annotation { "Feature Type Name" : "Feature", "Feature Type Description" : "" }
export const myFeature = defineFeature(function(context is Context, id is Id, definition is map)
    precondition{}
    {
        {
            var Q0;
            Q0=qCreatedBy(makeId("Top.planeOp"),FACE);
            var sketch = newSketch(context, id + "F0", { "sketchPlane" : qUnion([Q0])});
            skLineSegment(sketch, "E0.top", {"start": v(-5, 600) * mm, "end": v(-808, 600) * mm});
            skLineSegment(sketch, "E0.left", {"start": v(0, 0) * mm, "end": v(0, 595) * mm});
            skLineSegment(sketch, "E0.right", {"start": v(-813, 0) * mm, "end": v(-813, 595) * mm});
            skLineSegment(sketch, "E1.0", {"start": v(-811, 2) * mm, "end": v(-811, 596) * mm});
            skLineSegment(sketch, "E1.1", {"start": v(-4, 598) * mm, "end": v(-809, 598) * mm});
            skLineSegment(sketch, "E1.2", {"start": v(-2, 2) * mm, "end": v(-2, 596) * mm});
            skPoint(sketch, "E2.visualSharp", {"position": v(-813, 600) * mm});
            skArc(sketch, "E2.filletArc", {"start": v(-808, 600) * mm, "mid": v(-811.54, 598.54) * mm, "end": v(-813, 595) * mm});
            skPoint(sketch, "E3.visualSharp", {"position": v(-811, 598) * mm});
            skArc(sketch, "E3.filletArc", {"start": v(-809, 598) * mm, "mid": v(-810.41, 597.41) * mm, "end": v(-811, 596) * mm});
            skPoint(sketch, "E4.visualSharp", {"position": v(-2, 598) * mm});
            skArc(sketch, "E4.filletArc", {"start": v(-2, 596) * mm, "mid": v(-2.59, 597.41) * mm, "end": v(-4, 598) * mm});
            skPoint(sketch, "E5.visualSharp", {"position": v(0, 600) * mm});
            skArc(sketch, "E5.filletArc", {"start": v(0, 595) * mm, "mid": v(-1.46, 598.54) * mm, "end": v(-5, 600) * mm});
            skLineSegment(sketch, "E6", {"start": v(0, 0) * mm, "end": v(-2, 0) * mm});
            skLineSegment(sketch, "E7", {"start": v(-813, 0) * mm, "end": v(-811, 0) * mm});
            skLineSegment(sketch, "E8", {"start": v(0, 0) * mm, "end": v(-811, 0) * mm});
            skLineSegment(sketch, "E9.0", {"start": v(-2, 2) * mm, "end": v(-811, 2) * mm});
            skSolve(sketch);
        }
        {
            var Q0;
            Q0 = qSketchRegion(id + "F0", true);
            extrude(context, id + "F1", {"entities" : qUnion([Q0]), "depth" : 510 * mm});
        }
        {
            var Q0;
            Q0=makeQuery(id+"F1.opExtrude","SWEPT_FACE",FACE,{"disambiguationData":[OSD([sQuery(id+"F0.wireOp",EDGE,"E0.top")])]});
            var sketch = newSketch(context, id + "F2", { "sketchPlane" : qUnion([Q0])});
            skLineSegment(sketch, "E10", {"start": v(5, 510) * mm, "end": v(5, 1210) * mm});
            skLineSegment(sketch, "E11", {"start": v(5, 1210) * mm, "end": v(585, 1210) * mm});
            skLineSegment(sketch, "E12", {"start": v(585, 1210) * mm, "end": v(808, 510) * mm});
            skPoint(sketch, "E13.orphan", {"position": v(26.17, 1210) * mm});
            skLineSegment(sketch, "E14.0", {"start": v(55, 510) * mm, "end": v(55, 1110) * mm});
            skLineSegment(sketch, "E14.2", {"start": v(559.55, 1125.18) * mm, "end": v(755.52, 510) * mm});
            skLineSegment(sketch, "E14.3", {"start": v(105, 1160) * mm, "end": v(511.9, 1160) * mm});
            skPoint(sketch, "E15.visualSharp", {"position": v(55, 1160) * mm});
            skArc(sketch, "E15.filletArc", {"start": v(105, 1160) * mm, "mid": v(69.64, 1145.36) * mm, "end": v(55, 1110) * mm});
            skPoint(sketch, "E16.visualSharp", {"position": v(548.45, 1160) * mm});
            skArc(sketch, "E16.filletArc", {"start": v(559.55, 1125.18) * mm, "mid": v(541.41, 1150.37) * mm, "end": v(511.9, 1160) * mm});
            skPoint(sketch, "E17.visualSharp", {"position": v(738.8, 562.5) * mm});
            skPoint(sketch, "E18.visualSharp", {"position": v(55, 560) * mm});
            skLineSegment(sketch, "E19", {"start": v(808, 510) * mm, "end": v(5, 510) * mm});
            skSolve(sketch);
        }
        {
            var Q0;
            Q0=makeQuery(id+"F2.imprint","IMPRINT",FACE,{"disambiguationData":[TD([[makeQuery(id+"F2.imprint","IMPRINT",EDGE,{"derivedFrom":sQuery(id+"F2.wireOp",EDGE,"E10")}),-1.0]])]});
            extrude(context, id + "F3", {"entities" : qUnion([Q0]), "oppositeDirection" : true, "depth" : 2 * mm});
        }
        {
            var Q0;
            Q0=makeQuery(id+"F3.opExtrude","SWEPT_FACE",FACE,{"disambiguationData":[OSD([sQuery(id+"F2.wireOp",EDGE,"E12")])]});
            var sketch = newSketch(context, id + "F4", { "sketchPlane" : qUnion([Q0])});
            skLineSegment(sketch, "E20.bottom", {"start": v(-598, 240.68) * mm, "end": v(0, 240.68) * mm});
            skLineSegment(sketch, "E20.left", {"start": v(-598, 240.68) * mm, "end": v(-598, 975.34) * mm});
            skPoint(sketch, "E21.visualSharp", {"position": v(-50, 375.25) * mm});
            skPoint(sketch, "E22.visualSharp", {"position": v(-515.94, 338.49) * mm});
            skPoint(sketch, "E23.orphan", {"position": v(-498, 371.42) * mm});
            skPoint(sketch, "E24.2.start.orphan", {"position": v(-299, 371.42) * mm});
            skPoint(sketch, "E21.filletArc.start.orphan", {"position": v(-100, 371.42) * mm});
            skPoint(sketch, "E25.newPointB", {"position": v(-548, 579.34) * mm});
            skLineSegment(sketch, "E26", {"start": v(-299, 240.68) * mm, "end": v(-299, 1313.82) * mm, "construction": true});
            skLineSegment(sketch, "E27.MirrorCS", {"start": v(0, 240.68) * mm, "end": v(0, 975.34) * mm});
            skLineSegment(sketch, "E28", {"start": v(-299, 829.34) * mm, "end": v(135.66, 829.34) * mm, "construction": true});
            skLineSegment(sketch, "E29.MirrorCS", {"start": v(-548, 625.51) * mm, "end": v(-548, 919.34) * mm});
            skLineSegment(sketch, "E30.MirrorCS", {"start": v(-299, 574.92) * mm, "end": v(-498, 574.92) * mm});
            skArc(sketch, "E31.MirrorCS", {"start": v(-498, 574.92) * mm, "mid": v(-533.36, 589.57) * mm, "end": v(-548, 624.92) * mm});
            skLineSegment(sketch, "E32", {"start": v(-299, 969.34) * mm, "end": v(-498, 969.34) * mm});
            skPoint(sketch, "E33.newPointA", {"position": v(-959.05, 968.75) * mm});
            skArc(sketch, "E34.filletArc", {"start": v(-498, 969.34) * mm, "mid": v(-533.36, 954.7) * mm, "end": v(-548, 919.34) * mm});
            skLineSegment(sketch, "E35", {"start": v(-299, 969.34) * mm, "end": v(-299, 1019.34) * mm});
            skLineSegment(sketch, "E36", {"start": v(-299, 1019.34) * mm, "end": v(-554, 1019.34) * mm});
            skPoint(sketch, "E37.orphan", {"position": v(-598, 975.34) * mm});
            skLineSegment(sketch, "E38", {"start": v(-598, 975.34) * mm, "end": v(-554, 1019.34) * mm});
            skLineSegment(sketch, "E39.MirrorCS", {"start": v(0, 975.34) * mm, "end": v(-44, 1019.34) * mm});
            skLineSegment(sketch, "E40.MirrorCS", {"start": v(-299, 1019.34) * mm, "end": v(-44, 1019.34) * mm});
            skLineSegment(sketch, "E41.MirrorCS", {"start": v(-299, 969.34) * mm, "end": v(-100, 969.34) * mm});
            skArc(sketch, "E42.MirrorCS", {"start": v(-100, 969.34) * mm, "mid": v(-64.64, 954.7) * mm, "end": v(-50, 919.34) * mm});
            skLineSegment(sketch, "E43.MirrorCS", {"start": v(-50, 625.51) * mm, "end": v(-50, 919.34) * mm});
            skArc(sketch, "E44.MirrorCS", {"start": v(-100, 574.92) * mm, "mid": v(-64.64, 589.57) * mm, "end": v(-50, 624.92) * mm});
            skLineSegment(sketch, "E45.MirrorCS", {"start": v(-299, 574.92) * mm, "end": v(-100, 574.92) * mm});
            skSolve(sketch);
        }
        {
            var Q0;
            Q0=makeQuery(id+"F4.imprint","IMPRINT",FACE,{"disambiguationData":[TD([[makeQuery(id+"F4.imprint","IMPRINT",EDGE,{"derivedFrom":sQuery(id+"F4.wireOp",EDGE,"E20.bottom")}),1.0]])]});
            extrude(context, id + "F5", {"entities" : qUnion([Q0]), "depth" : 2 * mm});
        }
        {
            var Q0;
            Q0=qCreatedBy(makeId("Top.planeOp"),FACE);
            var sketch = newSketch(context, id + "F6", { "sketchPlane" : qUnion([Q0])});
            skLineSegment(sketch, "E46.bottom", {"start": v(0, 0) * mm, "end": v(805, 0) * mm});
            skLineSegment(sketch, "E46.top", {"start": v(0, 600) * mm, "end": v(805, 600) * mm});
            skLineSegment(sketch, "E46.left", {"start": v(0, 0) * mm, "end": v(0, 600) * mm});
            skLineSegment(sketch, "E46.right", {"start": v(805, 0) * mm, "end": v(805, 600) * mm});
            skSolve(sketch);
        }
        {
            var Q0;
            Q0 = qSketchRegion(id + "F6", true);
            extrude(context, id + "F7", {"entities" : qUnion([Q0]), "depth" : 465 * mm, "offsetDistance" : 25 * mm});
        }
        {
            var Q0;
            Q0=makeQuery(id+"F7.opExtrude","CAP_FACE",FACE,{"disambiguationData":[OSD([sQuery(id+"F6.wireOp",EDGE,"E46.bottom"),sQuery(id+"F6.wireOp",EDGE,"E46.top"),sQuery(id+"F6.wireOp",EDGE,"E46.left"),sQuery(id+"F6.wireOp",EDGE,"E46.right")])],"isStart":true});
            var Q1;
            Q1=makeQuery(id+"F7.opExtrude","SWEPT_FACE",FACE,{"disambiguationData":[OSD([sQuery(id+"F6.wireOp",EDGE,"E46.right")])]});
            var Q2;
            Q2=makeQuery(id+"F7.opExtrude","CAP_FACE",FACE,{"disambiguationData":[OSD([sQuery(id+"F6.wireOp",EDGE,"E46.bottom"),sQuery(id+"F6.wireOp",EDGE,"E46.top"),sQuery(id+"F6.wireOp",EDGE,"E46.left"),sQuery(id+"F6.wireOp",EDGE,"E46.right")])],"isStart":false});
            var Q3;
            Q3=makeQuery(id+"F7.opExtrude","SWEPT_FACE",FACE,{"disambiguationData":[OSD([sQuery(id+"F6.wireOp",EDGE,"E46.top")])]});
            var Q4;
            Q4=makeQuery(id+"F7.opExtrude","SWEPT_FACE",FACE,{"disambiguationData":[OSD([sQuery(id+"F6.wireOp",EDGE,"E46.left")])]});
            shell(context, id + "F8", {"entities" : qUnion([Q0, Q1, Q2, Q3, Q4]), "thickness" : (2) * mm});
        }
        {
            var Q0;
            Q0=qCreatedBy(makeId("Top.planeOp"),FACE);
            var sketch = newSketch(context, id + "F9", { "sketchPlane" : qUnion([Q0])});
            skLineSegment(sketch, "E47.bottom", {"start": v(-59.87, -24.6) * mm, "end": v(-40.87, -24.6) * mm});
            skLineSegment(sketch, "E47.top", {"start": v(-59.87, -74.6) * mm, "end": v(-40.87, -74.6) * mm});
            skLineSegment(sketch, "E47.left", {"start": v(-62.87, -27.6) * mm, "end": v(-62.87, -71.6) * mm});
            skLineSegment(sketch, "E47.right", {"start": v(-37.87, -27.6) * mm, "end": v(-37.87, -71.6) * mm});
            skPoint(sketch, "E48.visualSharp", {"position": v(-62.87, -24.6) * mm});
            skArc(sketch, "E48.filletArc", {"start": v(-59.87, -24.6) * mm, "mid": v(-62, -25.49) * mm, "end": v(-62.87, -27.6) * mm});
            skPoint(sketch, "E49.visualSharp", {"position": v(-37.87, -24.6) * mm});
            skArc(sketch, "E49.filletArc", {"start": v(-37.87, -27.6) * mm, "mid": v(-38.75, -25.49) * mm, "end": v(-40.87, -24.6) * mm});
            skPoint(sketch, "E50.visualSharp", {"position": v(-37.87, -74.6) * mm});
            skArc(sketch, "E50.filletArc", {"start": v(-40.87, -74.6) * mm, "mid": v(-38.75, -73.73) * mm, "end": v(-37.87, -71.6) * mm});
            skPoint(sketch, "E51.visualSharp", {"position": v(-62.87, -74.6) * mm});
            skArc(sketch, "E51.filletArc", {"start": v(-62.87, -71.6) * mm, "mid": v(-62, -73.73) * mm, "end": v(-59.87, -74.6) * mm});
            skArc(sketch, "E52.0", {"start": v(-59.87, -26.6) * mm, "mid": v(-60.58, -26.9) * mm, "end": v(-60.87, -27.6) * mm});
            skLineSegment(sketch, "E52.1", {"start": v(-59.87, -26.6) * mm, "end": v(-40.87, -26.6) * mm});
            skLineSegment(sketch, "E52.2", {"start": v(-60.87, -27.6) * mm, "end": v(-60.87, -71.6) * mm});
            skArc(sketch, "E52.3", {"start": v(-39.87, -27.6) * mm, "mid": v(-40.17, -26.9) * mm, "end": v(-40.87, -26.6) * mm});
            skArc(sketch, "E52.4", {"start": v(-60.87, -71.6) * mm, "mid": v(-60.58, -72.31) * mm, "end": v(-59.87, -72.6) * mm});
            skLineSegment(sketch, "E52.5", {"start": v(-59.87, -72.6) * mm, "end": v(-40.87, -72.6) * mm});
            skArc(sketch, "E52.6", {"start": v(-40.87, -72.6) * mm, "mid": v(-40.17, -72.31) * mm, "end": v(-39.87, -71.6) * mm});
            skLineSegment(sketch, "E52.7", {"start": v(-39.87, -27.6) * mm, "end": v(-39.87, -71.6) * mm});
            skSolve(sketch);
        }
        {
            var Q0;
            Q0 = qSketchRegion(id + "F9", true);
            var Q1;
            Q1=makeQuery(id+"F9.imprint","IMPRINT",FACE,{"disambiguationData":[TD([[makeQuery(id+"F9.imprint","IMPRINT",EDGE,{"derivedFrom":sQuery(id+"F9.wireOp",EDGE,"E47.bottom")}),-1.0]])]});
            extrude(context, id + "F10", {"entities" : qUnion([Q0, Q1]), "depth" : 1040 * mm});
        }
        {
            var Q0;
            Q0=makeQuery(id+"F1.opExtrude","SWEPT_FACE",FACE,{"disambiguationData":[OSD([sQuery(id+"F0.wireOp",EDGE,"E7"),sQuery(id+"F0.wireOp",EDGE,"E8")])]});
            var sketch = newSketch(context, id + "F11", { "sketchPlane" : qUnion([Q0])});
            skLineSegment(sketch, "E53", {"start": v(0, 510) * mm, "end": v(-315.52, 510) * mm});
            skLineSegment(sketch, "E54", {"start": v(-538, 106.26) * mm, "end": v(-713, 106.26) * mm});
            skLineSegment(sketch, "E55", {"start": v(-763, 156.26) * mm, "end": v(-763, 510) * mm});
            skPoint(sketch, "E56.visualSharp", {"position": v(-406.5, 510) * mm});
            skPoint(sketch, "E57.visualSharp", {"position": v(-14.07, 106.26) * mm});
            skPoint(sketch, "E58.visualSharp", {"position": v(-763, 106.26) * mm});
            skArc(sketch, "E58.filletArc", {"start": v(-763, 156.26) * mm, "mid": v(-748.36, 120.9) * mm, "end": v(-713, 106.26) * mm});
            skLineSegment(sketch, "E59", {"start": v(-362.25, 477.77) * mm, "end": v(-491.26, 138.49) * mm});
            skPoint(sketch, "E60.visualSharp", {"position": v(-350, 510) * mm});
            skArc(sketch, "E60.filletArc", {"start": v(-315.52, 510) * mm, "mid": v(-343.9, 501.16) * mm, "end": v(-362.25, 477.77) * mm});
            skArc(sketch, "E61.filletArc", {"start": v(-538, 106.26) * mm, "mid": v(-509.61, 115.1) * mm, "end": v(-491.26, 138.49) * mm});
            skSolve(sketch);
        }
        {
            var Q0;
            Q0 = qSketchRegion(id + "F11", true);
            var Q1;
            Q1=makeQuery(id+"F11.imprint","IMPRINT",FACE,{"disambiguationData":[TD([[makeQuery(id+"F11.imprint","IMPRINT",EDGE,{"derivedFrom":sQuery(id+"F11.wireOp",EDGE,"Jq7AXQ9a-MJNj-Bxrc-Dwik-De4Gg8XfQ3kM")}),-1.0]])]});
            var Q2;
            Q2=makeQuery(id+"F11.imprint","IMPRINT",FACE,{"disambiguationData":[TD([[makeQuery(id+"F11.imprint","IMPRINT",EDGE,{"derivedFrom":sQuery(id+"F11.wireOp",EDGE,"E54")}),-1.0]])]});
            var Q3;
            Q3=makeQuery(id+"F1.opExtrude","SWEPT_FACE",FACE,{"disambiguationData":[OSD([sQuery(id+"F0.wireOp",EDGE,"E1.1")])]});
            extrude(context, id + "F12", {"entities" : qUnion([Q0, Q1, Q2]), "operationType" : NewBodyOperationType.REMOVE, "endBound" : BoundingType.UP_TO_SURFACE, "oppositeDirection" : true, "endBoundEntityFace" : qUnion([Q3]), "depth" : 25 * mm});
        }
        {
            var Q0;
            Q0=makeQuery(id+"F1.opExtrude","SWEPT_FACE",FACE,{"disambiguationData":[OSD([sQuery(id+"F0.wireOp",EDGE,"E0.right")])]});
            var sketch = newSketch(context, id + "F13", { "sketchPlane" : qUnion([Q0])});
            skLineSegment(sketch, "E62", {"start": v(-595, 510) * mm, "end": v(-595, 1196.55) * mm});
            skLineSegment(sketch, "E63", {"start": v(-595, 1196.55) * mm, "end": v(-595, 1203.08) * mm});
            skLineSegment(sketch, "E64", {"start": v(-595, 1203.08) * mm, "end": v(-611.4, 1194.32) * mm});
            skLineSegment(sketch, "E65", {"start": v(-611.4, 1194.32) * mm, "end": v(-537.5, 1262.48) * mm});
            skLineSegment(sketch, "E66", {"start": v(-537.5, 1262.48) * mm, "end": v(-510.53, 1287.36) * mm});
            skLineSegment(sketch, "E67", {"start": v(-297.5, 510) * mm, "end": v(-297.5, 1399.73) * mm});
            skLineSegment(sketch, "E68", {"start": v(-510.53, 1287.36) * mm, "end": v(-323.46, 1287.36) * mm});
            skLineSegment(sketch, "E69", {"start": v(-323.46, 1287.36) * mm, "end": v(-297.5, 1287.36) * mm});
            skLineSegment(sketch, "E70", {"start": v(-297.5, 1287.36) * mm, "end": v(-297.5, 1305.9) * mm});
            skLineSegment(sketch, "E71.0", {"start": v(-323.46, 1289.36) * mm, "end": v(-297.5, 1289.36) * mm});
            skLineSegment(sketch, "E71.1", {"start": v(-511.31, 1289.36) * mm, "end": v(-323.46, 1289.36) * mm});
            skLineSegment(sketch, "E71.2", {"start": v(-538.86, 1263.95) * mm, "end": v(-511.31, 1289.36) * mm});
            skLineSegment(sketch, "E72.0", {"start": v(-612.76, 1195.8) * mm, "end": v(-538.86, 1263.95) * mm});
            skLineSegment(sketch, "E73.MirrorCS", {"start": v(0, 1196.55) * mm, "end": v(0, 1203.08) * mm});
            skLineSegment(sketch, "E74.MirrorCS", {"start": v(-57.5, 1262.48) * mm, "end": v(-84.47, 1287.36) * mm});
            skLineSegment(sketch, "E75.MirrorCS", {"start": v(16.4, 1194.32) * mm, "end": v(-57.5, 1262.48) * mm});
            skLineSegment(sketch, "E76.MirrorCS", {"start": v(-56.14, 1263.95) * mm, "end": v(-83.69, 1289.36) * mm});
            skLineSegment(sketch, "E77.MirrorCS", {"start": v(17.76, 1195.8) * mm, "end": v(-56.14, 1263.95) * mm});
            skLineSegment(sketch, "E78.MirrorCS", {"start": v(-83.69, 1289.36) * mm, "end": v(-271.54, 1289.36) * mm});
            skLineSegment(sketch, "E79.MirrorCS", {"start": v(0, 1203.08) * mm, "end": v(16.4, 1194.32) * mm});
            skLineSegment(sketch, "E80.MirrorCS", {"start": v(-271.54, 1289.36) * mm, "end": v(-297.5, 1289.36) * mm});
            skLineSegment(sketch, "E81.MirrorCS", {"start": v(-84.47, 1287.36) * mm, "end": v(-271.54, 1287.36) * mm});
            skLineSegment(sketch, "E82.MirrorCS", {"start": v(-271.54, 1287.36) * mm, "end": v(-297.5, 1287.36) * mm});
            skLineSegment(sketch, "E83", {"start": v(16.4, 1194.32) * mm, "end": v(17.76, 1195.8) * mm});
            skLineSegment(sketch, "E84", {"start": v(-612.76, 1195.8) * mm, "end": v(-611.4, 1194.32) * mm});
            skSolve(sketch);
        }
        {
            var Q0;
            Q0=makeQuery(id+"F13.imprint","IMPRINT",FACE,{"disambiguationData":[TD([[makeQuery(id+"F13.imprint","IMPRINT",EDGE,{"derivedFrom":sQuery(id+"F13.wireOp",EDGE,"E74.MirrorCS")}),-1.0]])]});
            var Q1;
            Q1=makeQuery(id+"F13.imprint","IMPRINT",FACE,{"disambiguationData":[TD([[makeQuery(id+"F13.imprint","IMPRINT",EDGE,{"derivedFrom":sQuery(id+"F13.wireOp",EDGE,"E65")}),1.0]])]});
            extrude(context, id + "F14", {"entities" : qUnion([Q0, Q1]), "oppositeDirection" : true, "depth" : 600 * mm});
        }
        {
            var Q0;
            Q0=makeQuery(id+"F7.opExtrude","SWEPT_FACE",FACE,{"disambiguationData":[OSD([sQuery(id+"F6.wireOp",EDGE,"E46.bottom")])]});
            var sketch = newSketch(context, id + "F15", { "sketchPlane" : qUnion([Q0])});
            skLineSegment(sketch, "E85", {"start": v(402.5, 0) * mm, "end": v(402.5, 380) * mm, "construction": true});
            skLineSegment(sketch, "E86", {"start": v(402.5, 380) * mm, "end": v(402.5, 190) * mm, "construction": true});
            skLineSegment(sketch, "E87", {"start": v(402.5, 190) * mm, "end": v(402.5, 285) * mm});
            skLineSegment(sketch, "E88", {"start": v(402.5, 285) * mm, "end": v(102.5, 285) * mm, "construction": true});
            skLineSegment(sketch, "E89.MirrorCS", {"start": v(402.5, 285) * mm, "end": v(702.5, 285) * mm, "construction": true});
            skText(sketch, "E90", { "text": "Fixby Hall Works\nBreakdown Gang\n", "fontName": "AllertaStencil-Regular.ttf"});
            skCircle(sketch, "E91", {"center": v(402.5, 173.4) * mm, "radius": 10 * mm});
            skCircle(sketch, "E92.0.1.0", {"center": v(402.5, 53.4) * mm, "radius": 10 * mm});
            skCircle(sketch, "E92.1.0.0", {"center": v(462.5, 173.4) * mm, "radius": 10 * mm});
            skCircle(sketch, "E92.1.1.0", {"center": v(462.5, 53.4) * mm, "radius": 10 * mm});
            skCircle(sketch, "E92.2.0.0", {"center": v(522.5, 173.4) * mm, "radius": 10 * mm});
            skCircle(sketch, "E92.2.1.0", {"center": v(522.5, 53.4) * mm, "radius": 10 * mm});
            skCircle(sketch, "E92.3.0.0", {"center": v(582.5, 173.4) * mm, "radius": 10 * mm});
            skCircle(sketch, "E92.3.1.0", {"center": v(582.5, 53.4) * mm, "radius": 10 * mm});
            skCircle(sketch, "E92.4.0.0", {"center": v(642.5, 173.4) * mm, "radius": 10 * mm});
            skCircle(sketch, "E92.4.1.0", {"center": v(642.5, 53.4) * mm, "radius": 10 * mm});
            skLineSegment(sketch, "E92.direction1", {"start": v(402.5, 173.4) * mm, "end": v(462.5, 173.4) * mm, "construction": true});
            skLineSegment(sketch, "E92.direction2", {"start": v(402.5, 173.4) * mm, "end": v(402.5, 53.4) * mm, "construction": true});
            skLineSegment(sketch, "E93", {"start": v(462.5, 173.4) * mm, "end": v(402.5, 173.4) * mm});
            skLineSegment(sketch, "E94", {"start": v(432.5, 173.4) * mm, "end": v(432.5, 113.4) * mm});
            skCircle(sketch, "E95", {"center": v(432.5, 113.4) * mm, "radius": 10 * mm});
            skCircle(sketch, "E96.1.0.0", {"center": v(492.5, 113.4) * mm, "radius": 10 * mm});
            skCircle(sketch, "E96.2.0.0", {"center": v(552.5, 113.4) * mm, "radius": 10 * mm});
            skCircle(sketch, "E96.3.0.0", {"center": v(612.5, 113.4) * mm, "radius": 10 * mm});
            skCircle(sketch, "E96.4.0.0", {"center": v(672.5, 113.4) * mm, "radius": 10 * mm});
            skLineSegment(sketch, "E96.direction1", {"start": v(432.5, 113.4) * mm, "end": v(492.5, 113.4) * mm, "construction": true});
            skCircle(sketch, "E97.MirrorC", {"center": v(342.5, 173.4) * mm, "radius": 10 * mm});
            skCircle(sketch, "E98.MirrorC", {"center": v(222.5, 53.4) * mm, "radius": 10 * mm});
            skCircle(sketch, "E99.MirrorC", {"center": v(312.5, 113.4) * mm, "radius": 10 * mm});
            skCircle(sketch, "E100.MirrorC", {"center": v(252.5, 113.4) * mm, "radius": 10 * mm});
            skCircle(sketch, "E101.MirrorC", {"center": v(192.5, 113.4) * mm, "radius": 10 * mm});
            skCircle(sketch, "E102.MirrorC", {"center": v(132.5, 113.4) * mm, "radius": 10 * mm});
            skCircle(sketch, "E103.MirrorC", {"center": v(342.5, 53.4) * mm, "radius": 10 * mm});
            skCircle(sketch, "E104.MirrorC", {"center": v(282.5, 173.4) * mm, "radius": 10 * mm});
            skCircle(sketch, "E105.MirrorC", {"center": v(282.5, 53.4) * mm, "radius": 10 * mm});
            skCircle(sketch, "E106.MirrorC", {"center": v(222.5, 173.4) * mm, "radius": 10 * mm});
            skCircle(sketch, "E107.MirrorC", {"center": v(162.5, 173.4) * mm, "radius": 10 * mm});
            skCircle(sketch, "E108.MirrorC", {"center": v(162.5, 53.4) * mm, "radius": 10 * mm});
            skLineSegment(sketch, "E109.MirrorCS", {"start": v(372.5, 173.4) * mm, "end": v(372.5, 113.4) * mm});
            skLineSegment(sketch, "E110.MirrorCS", {"start": v(372.5, 113.4) * mm, "end": v(312.5, 113.4) * mm, "construction": true});
            skCircle(sketch, "E111", {"center": v(372.5, 113.4) * mm, "radius": 10 * mm});
            skLineSegment(sketch, "E112.top", {"start": v(0, 70) * mm, "end": v(35, 70) * mm});
            skLineSegment(sketch, "E112.right", {"start": v(40, 0) * mm, "end": v(40, 65) * mm});
            skPoint(sketch, "E113.visualSharp", {"position": v(40, 70) * mm});
            skArc(sketch, "E113.filletArc", {"start": v(40, 65) * mm, "mid": v(38.54, 68.54) * mm, "end": v(35, 70) * mm});
            const initialGuessF15  = {"E90": [0.1025, 0.285, 1, 0, 0.05015]};
            skSetInitialGuess(sketch, initialGuessF15);
            skSolve(sketch);
        }
        {
            var Q0;
            Q0 = qSketchRegion(id + "F15", true);
            extrude(context, id + "F16", {"entities" : qUnion([Q0]), "operationType" : NewBodyOperationType.REMOVE, "oppositeDirection" : true, "depth" : 25 * mm});
        }
        {
            var Q0;
            Q0=makeQuery(id+"F1.opExtrude","SWEPT_FACE",FACE,{"disambiguationData":[OSD([sQuery(id+"F0.wireOp",EDGE,"E0.right")])]});
            var sketch = newSketch(context, id + "F17", { "sketchPlane" : qUnion([Q0])});
            skLineSegment(sketch, "E114", {"start": v(-297.5, 500) * mm, "end": v(-297.5, 0) * mm, "construction": true});
            skLineSegment(sketch, "E115", {"start": v(-297.5, 500) * mm, "end": v(-297.5, 415) * mm, "construction": true});
            skLineSegment(sketch, "E116", {"start": v(-297.5, 415) * mm, "end": v(-595, 415) * mm, "construction": true});
            skLineSegment(sketch, "E117", {"start": v(-446.25, 415) * mm, "end": v(-595, 415) * mm});
            skLineSegment(sketch, "E118", {"start": v(-520.63, 415) * mm, "end": v(-520.63, 500) * mm, "construction": true});
            skCircle(sketch, "E119", {"center": v(-520.63, 415) * mm, "radius": 6 * mm});
            skLineSegment(sketch, "E120", {"start": v(-520.63, 415) * mm, "end": v(-595, 415) * mm});
            skCircle(sketch, "E121", {"center": v(-557.81, 415) * mm, "radius": 6 * mm});
            skLineSegment(sketch, "E122", {"start": v(-520.63, 415) * mm, "end": v(-520.63, 457.5) * mm});
            skCircle(sketch, "E123", {"center": v(-520.63, 457.5) * mm, "radius": 6 * mm});
            skSolve(sketch);
        }
        {
            var Q0;
            Q0=makeQuery(id+"F17.imprint","IMPRINT",FACE,{"disambiguationData":[TD([[makeQuery(id+"F17.imprint","IMPRINT",EDGE,{"derivedFrom":sQuery(id+"F17.wireOp",EDGE,"E123")}),-1.0]])]});
            var sketch = newSketch(context, id + "F18", { "sketchPlane" : qUnion([Q0])});
            skLineSegment(sketch, "E124.bottom", {"start": v(-742.96, 0) * mm, "end": v(-762.96, 0) * mm});
            skLineSegment(sketch, "E124.top", {"start": v(-742.96, 295) * mm, "end": v(-762.96, 295) * mm});
            skLineSegment(sketch, "E124.left", {"start": v(-742.96, 0) * mm, "end": v(-742.96, 295) * mm});
            skLineSegment(sketch, "E124.right", {"start": v(-762.96, 0) * mm, "end": v(-762.96, 295) * mm});
            skSolve(sketch);
        }
        {
            var Q0;
            Q0 = qSketchRegion(id + "F18", true);
            extrude(context, id + "F19", {"entities" : qUnion([Q0]), "depth" : 20 * mm});
        }
        {
            var Q0;
            Q0=makeQuery(id+"F19.opExtrude","SWEPT_FACE",FACE,{"disambiguationData":[OSD([sQuery(id+"F18.wireOp",EDGE,"E124.top")])]});
            var Q1;
            Q1=makeQuery(id+"F19.opExtrude","SWEPT_FACE",FACE,{"disambiguationData":[OSD([sQuery(id+"F18.wireOp",EDGE,"E124.bottom")])]});
            shell(context, id + "F20", {"entities" : qUnion([Q0, Q1]), "thickness" : 2 * mm});
        }
        {
            var Q0;
            Q0=makeQuery(id+"F19.opExtrude","CAP_FACE",FACE,{"disambiguationData":[OSD([sQuery(id+"F18.wireOp",EDGE,"E124.bottom"),sQuery(id+"F18.wireOp",EDGE,"E124.top"),sQuery(id+"F18.wireOp",EDGE,"E124.left"),sQuery(id+"F18.wireOp",EDGE,"E124.right")])],"isStart":false});
            var sketch = newSketch(context, id + "F21", { "sketchPlane" : qUnion([Q0])});
            skLineSegment(sketch, "E125.bottom", {"start": v(-828.15, 0) * mm, "end": v(-848.15, 0) * mm});
            skLineSegment(sketch, "E125.top", {"start": v(-828.15, 355) * mm, "end": v(-848.15, 355) * mm});
            skLineSegment(sketch, "E125.left", {"start": v(-828.15, 0) * mm, "end": v(-828.15, 355) * mm});
            skLineSegment(sketch, "E125.right", {"start": v(-848.15, 0) * mm, "end": v(-848.15, 355) * mm});
            skSolve(sketch);
        }
        {
            var Q0;
            Q0 = qSketchRegion(id + "F21", true);
            extrude(context, id + "F22", {"entities" : qUnion([Q0]), "depth" : 20 * mm});
        }
        {
            var Q0;
            Q0=makeQuery(id+"F22.opExtrude","SWEPT_FACE",FACE,{"disambiguationData":[OSD([sQuery(id+"F21.wireOp",EDGE,"E125.bottom")])]});
            var Q1;
            Q1=makeQuery(id+"F22.opExtrude","SWEPT_FACE",FACE,{"disambiguationData":[OSD([sQuery(id+"F21.wireOp",EDGE,"E125.top")])]});
            shell(context, id + "F23", {"entities" : qUnion([Q0, Q1]), "thickness" : 2 * mm});
        }
        {
            var Q0;
            Q0=makeQuery(id+"F17.imprint","IMPRINT",FACE,{"disambiguationData":[TD([[makeQuery(id+"F17.imprint","IMPRINT",EDGE,{"derivedFrom":sQuery(id+"F17.wireOp",EDGE,"E123")}),-1.0]])]});
            var sketch = newSketch(context, id + "F24", { "sketchPlane" : qUnion([Q0])});
            skLineSegment(sketch, "E126.bottom", {"start": v(-81.45, 523.79) * mm, "end": v(-884.45, 523.79) * mm});
            skLineSegment(sketch, "E126.top", {"start": v(-81.45, 503.79) * mm, "end": v(-884.45, 503.79) * mm});
            skLineSegment(sketch, "E126.left", {"start": v(-81.45, 523.79) * mm, "end": v(-81.45, 503.79) * mm});
            skLineSegment(sketch, "E126.right", {"start": v(-884.45, 523.79) * mm, "end": v(-884.45, 503.79) * mm});
            skSolve(sketch);
        }
        {
            var Q0;
            Q0 = qSketchRegion(id + "F24", true);
            extrude(context, id + "F25", {"entities" : qUnion([Q0]), "depth" : 20 * mm});
        }
        {
            var Q0;
            Q0=makeQuery(id+"F25.opExtrude","SWEPT_FACE",FACE,{"disambiguationData":[OSD([sQuery(id+"F24.wireOp",EDGE,"E126.left")])]});
            var Q1;
            Q1=makeQuery(id+"F25.opExtrude","SWEPT_FACE",FACE,{"disambiguationData":[OSD([sQuery(id+"F24.wireOp",EDGE,"E126.right")])]});
            shell(context, id + "F26", {"entities" : qUnion([Q0, Q1]), "thickness" : 2 * mm});
        }
        {
            var Q0;
            Q0=makeQuery(id+"F4.imprint","IMPRINT",FACE,{"disambiguationData":[TD([[makeQuery(id+"F4.imprint","IMPRINT",EDGE,{"derivedFrom":sQuery(id+"F4.wireOp",EDGE,"E20.bottom")}),1.0]])]});
            var sketch = newSketch(context, id + "F27", { "sketchPlane" : qUnion([Q0])});
            skLineSegment(sketch, "E127", {"start": v(-300.19, 969.34) * mm, "end": v(-100.35, 969.34) * mm});
            skLineSegment(sketch, "E128", {"start": v(-50.35, 919.34) * mm, "end": v(-50.35, 569.34) * mm});
            skLineSegment(sketch, "E129", {"start": v(-100.35, 519.34) * mm, "end": v(-300.19, 519.34) * mm});
            skPoint(sketch, "E130.visualSharp", {"position": v(-50.35, 969.34) * mm});
            skArc(sketch, "E130.filletArc", {"start": v(-50.35, 919.34) * mm, "mid": v(-65, 954.7) * mm, "end": v(-100.35, 969.34) * mm});
            skPoint(sketch, "E131.visualSharp", {"position": v(-50.35, 519.34) * mm});
            skArc(sketch, "E131.filletArc", {"start": v(-100.35, 519.34) * mm, "mid": v(-65, 533.98) * mm, "end": v(-50.35, 569.34) * mm});
            skLineSegment(sketch, "E132", {"start": v(-300.19, 969.34) * mm, "end": v(-300.19, 519.34) * mm, "construction": true});
            skLineSegment(sketch, "E133.MirrorCS", {"start": v(-297.81, 969.34) * mm, "end": v(-497.65, 969.34) * mm});
            skArc(sketch, "E134.MirrorCS", {"start": v(-547.65, 919.34) * mm, "mid": v(-533, 954.7) * mm, "end": v(-497.65, 969.34) * mm});
            skLineSegment(sketch, "E135.MirrorCS", {"start": v(-547.65, 919.34) * mm, "end": v(-547.65, 569.34) * mm});
            skArc(sketch, "E136.MirrorCS", {"start": v(-497.65, 519.34) * mm, "mid": v(-533, 533.98) * mm, "end": v(-547.65, 569.34) * mm});
            skLineSegment(sketch, "E137.MirrorCS", {"start": v(-497.65, 519.34) * mm, "end": v(-297.81, 519.34) * mm});
            skSolve(sketch);
        }
        {
            var Q0;
            Q0 = qSketchRegion(id + "F27", true);
            extrude(context, id + "F28", {"entities" : qUnion([Q0]), "operationType" : NewBodyOperationType.ADD, "depth" : 25 * mm});
        }
        {
            var Q0;
            {var subQ2=sQuery(id+"F27.wireOp",EDGE,"E127");Q0=makeQuery(id+"F27.imprint","IMPRINT",FACE,{"disambiguationData":[TD([[makeQuery(id+"F27.imprint","IMPRINT",EDGE,{"derivedFrom":subQ2}),-1.0]])]});}
            extrude(context, id + "F29", {"entities" : qUnion([Q0]), "operationType" : NewBodyOperationType.REMOVE, "endBound" : BoundingType.THROUGH_ALL, "depth" : 25 * mm});
        }
        {
            var Q0;
            Q0=makeQuery(id+"F5.opExtrude","SWEPT_BODY",BODY,{"disambiguationData":[OSD([sQuery(id+"F4.wireOp",EDGE,"E20.bottom"),sQuery(id+"F4.wireOp",EDGE,"E20.left"),sQuery(id+"F4.wireOp",EDGE,"E27.MirrorCS"),sQuery(id+"F4.wireOp",EDGE,"E36"),sQuery(id+"F4.wireOp",EDGE,"E38"),sQuery(id+"F4.wireOp",EDGE,"E39.MirrorCS"),sQuery(id+"F4.wireOp",EDGE,"E40.MirrorCS")])]});
            transform(context, id + "F30", {"entities" : qUnion([Q0]), "transformType" : TransformType.TRANSLATION_3D, "dx" : 150 * mm, "dy" : 0 * mm, "dz" : 0 * mm, "makeCopy" : true});
        }
        {
            var Q0;
            Q0=makeQuery(id+"F30.opPattern","COPY",FACE,{"derivedFrom":makeQuery(id+"F5.opExtrude","CAP_FACE",FACE,{"disambiguationData":[OSD([sQuery(id+"F4.wireOp",EDGE,"E20.bottom"),sQuery(id+"F4.wireOp",EDGE,"E20.left"),sQuery(id+"F4.wireOp",EDGE,"E27.MirrorCS"),sQuery(id+"F4.wireOp",EDGE,"E36"),sQuery(id+"F4.wireOp",EDGE,"E38"),sQuery(id+"F4.wireOp",EDGE,"E39.MirrorCS"),sQuery(id+"F4.wireOp",EDGE,"E40.MirrorCS")])],"isStart":true}),"instanceName":"1"});
            var sketch = newSketch(context, id + "F31", { "sketchPlane" : qUnion([Q0])});
            skLineSegment(sketch, "E138", {"start": v(50.35, 614.87) * mm, "end": v(50.35, 702.03) * mm});
            skLineSegment(sketch, "E139", {"start": v(100.35, 702.03) * mm, "end": v(497.65, 702.03) * mm});
            skLineSegment(sketch, "E140", {"start": v(547.65, 702.03) * mm, "end": v(547.65, 614.87) * mm});
            skLineSegment(sketch, "E141", {"start": v(100.35, 564.87) * mm, "end": v(497.65, 564.87) * mm});
            skArc(sketch, "E142.filletArc", {"start": v(497.65, 564.87) * mm, "mid": v(533, 579.51) * mm, "end": v(547.65, 614.87) * mm});
            skPoint(sketch, "E143.visualSharp", {"position": v(50.35, 564.87) * mm});
            skArc(sketch, "E143.filletArc", {"start": v(50.35, 614.87) * mm, "mid": v(65, 579.51) * mm, "end": v(100.35, 564.87) * mm});
            skPoint(sketch, "E144.visualSharp", {"position": v(50.35, 702.03) * mm});
            skArc(sketch, "E144.filletArc", {"start": v(50.35, 752.03) * mm, "mid": v(65, 716.67) * mm, "end": v(100.35, 702.03) * mm});
            skPoint(sketch, "E145.visualSharp", {"position": v(547.65, 702.03) * mm});
            skArc(sketch, "E145.filletArc", {"start": v(497.65, 702.03) * mm, "mid": v(533, 716.67) * mm, "end": v(547.65, 752.03) * mm});
            skSolve(sketch);
        }
        {
            var Q0;
            Q0=makeQuery(id+"F31.imprint","IMPRINT",FACE,{"disambiguationData":[TD([[makeQuery(id+"F31.imprint","IMPRINT",EDGE,{"derivedFrom":sQuery(id+"F31.wireOp",EDGE,"E138")}),1.0]])]});
            extrude(context, id + "F32", {"entities" : qUnion([Q0]), "operationType" : NewBodyOperationType.ADD, "oppositeDirection" : true, "depth" : 2 * mm});
        }
        {
            var Q0;
            Q0=makeQuery(id+"F32.boolean.opBoolean","MERGE",FACE,{"derivedFrom":[makeQuery(id+"F30.opPattern","COPY",FACE,{"derivedFrom":makeQuery(id+"F5.opExtrude","CAP_FACE",FACE,{"disambiguationData":[OSD([sQuery(id+"F4.wireOp",EDGE,"E20.bottom"),sQuery(id+"F4.wireOp",EDGE,"E20.left"),sQuery(id+"F4.wireOp",EDGE,"E27.MirrorCS"),sQuery(id+"F4.wireOp",EDGE,"E36"),sQuery(id+"F4.wireOp",EDGE,"E38"),sQuery(id+"F4.wireOp",EDGE,"E39.MirrorCS"),sQuery(id+"F4.wireOp",EDGE,"E40.MirrorCS")])],"isStart":true}),"instanceName":"1"}),makeQuery(id+"F32.opExtrude","CAP_FACE",FACE,{"disambiguationData":[OSD([sQuery(id+"F27.wireOp",EDGE,"E128"),sQuery(id+"F27.wireOp",EDGE,"E135.MirrorCS"),sQuery(id+"F31.wireOp",EDGE,"E138"),sQuery(id+"F31.wireOp",EDGE,"E139"),sQuery(id+"F31.wireOp",EDGE,"E140"),sQuery(id+"F31.wireOp",EDGE,"E141"),sQuery(id+"F31.wireOp",EDGE,"E142.filletArc"),sQuery(id+"F31.wireOp",EDGE,"E143.filletArc"),sQuery(id+"F31.wireOp",EDGE,"E144.filletArc"),sQuery(id+"F31.wireOp",EDGE,"E145.filletArc")])],"isStart":true})]});
            var sketch = newSketch(context, id + "F33", { "sketchPlane" : qUnion([Q0])});
            skLineSegment(sketch, "E146.bottom", {"start": v(0, 286.2) * mm, "end": v(598, 286.2) * mm});
            skLineSegment(sketch, "E146.top", {"start": v(0, 321.2) * mm, "end": v(598, 321.2) * mm});
            skLineSegment(sketch, "E146.left", {"start": v(0, 286.2) * mm, "end": v(0, 321.2) * mm});
            skLineSegment(sketch, "E146.right", {"start": v(598, 286.2) * mm, "end": v(598, 321.2) * mm});
            skSolve(sketch);
        }
        {
            var Q0;
            Q0 = qSketchRegion(id + "F33", true);
            extrude(context, id + "F34", {"entities" : qUnion([Q0]), "operationType" : NewBodyOperationType.REMOVE, "oppositeDirection" : true, "depth" : 25 * mm});
        }
        {
            var Q0;
            Q0=qCreatedBy(makeId("Right.planeOp"),FACE);
            var sketch = newSketch(context, id + "F35", { "sketchPlane" : qUnion([Q0])});
            skLineSegment(sketch, "E147.top", {"start": v(-624.5, 48.19) * mm, "end": v(-574.5, 48.19) * mm});
            skLineSegment(sketch, "E148", {"start": v(-624.5, 795.18) * mm, "end": v(-574.5, 795.18) * mm, "construction": true});
            skLineSegment(sketch, "E149", {"start": v(-624.5, 795.18) * mm, "end": v(-624.5, 785.18) * mm, "construction": true});
            skLineSegment(sketch, "E150", {"start": v(-599.5, 898.19) * mm, "end": v(-599.5, 848.19) * mm, "construction": true});
            skLineSegment(sketch, "E151", {"start": v(-599.5, 848.19) * mm, "end": v(-599.5, 795.18) * mm, "construction": true});
            skLineSegment(sketch, "E152", {"start": v(-599.5, 795.18) * mm, "end": v(-599.5, 785.18) * mm, "construction": true});
            skLineSegment(sketch, "E153", {"start": v(-599.5, 785.18) * mm, "end": v(-599.5, 735.18) * mm, "construction": true});
            skLineSegment(sketch, "E154", {"start": v(-599.5, 735.18) * mm, "end": v(-599.5, 725.18) * mm, "construction": true});
            skLineSegment(sketch, "E155", {"start": v(-599.5, 725.18) * mm, "end": v(-599.5, 675.18) * mm, "construction": true});
            skLineSegment(sketch, "E156", {"start": v(-599.5, 675.18) * mm, "end": v(-599.5, 665.18) * mm, "construction": true});
            skLineSegment(sketch, "E157", {"start": v(-599.5, 665.18) * mm, "end": v(-599.5, 615.18) * mm, "construction": true});
            skLineSegment(sketch, "E158", {"start": v(-599.5, 615.18) * mm, "end": v(-599.5, 565.18) * mm, "construction": true});
            skLineSegment(sketch, "E159", {"start": v(-599.5, 565.18) * mm, "end": v(-599.5, 515.18) * mm, "construction": true});
            skPoint(sketch, "E159.endSnap0", {"position": v(-599.5, 640.18) * mm});
            skLineSegment(sketch, "E160", {"start": v(-599.5, 515.18) * mm, "end": v(-599.5, 505.18) * mm, "construction": true});
            skLineSegment(sketch, "E161", {"start": v(-599.5, 505.18) * mm, "end": v(-599.5, 455.18) * mm, "construction": true});
            skLineSegment(sketch, "E162", {"start": v(-599.5, 455.18) * mm, "end": v(-599.5, 445.18) * mm, "construction": true});
            skLineSegment(sketch, "E163", {"start": v(-599.5, 445.18) * mm, "end": v(-599.5, 395.18) * mm, "construction": true});
            skLineSegment(sketch, "E164", {"start": v(-599.5, 395.18) * mm, "end": v(-599.5, 385.18) * mm, "construction": true});
            skLineSegment(sketch, "E165", {"start": v(-599.5, 385.18) * mm, "end": v(-599.5, 335.18) * mm, "construction": true});
            skLineSegment(sketch, "E166", {"start": v(-599.5, 335.18) * mm, "end": v(-599.5, 325.18) * mm, "construction": true});
            skLineSegment(sketch, "E167", {"start": v(-599.5, 325.18) * mm, "end": v(-599.5, 275.18) * mm, "construction": true});
            skLineSegment(sketch, "E168", {"start": v(-599.5, 275.18) * mm, "end": v(-599.5, 265.18) * mm, "construction": true});
            skLineSegment(sketch, "E169", {"start": v(-599.5, 265.18) * mm, "end": v(-599.5, 215.18) * mm, "construction": true});
            skLineSegment(sketch, "E170", {"start": v(-599.5, 215.18) * mm, "end": v(-599.5, 205.18) * mm, "construction": true});
            skLineSegment(sketch, "E171", {"start": v(-599.5, 205.18) * mm, "end": v(-599.5, 155.18) * mm, "construction": true});
            skLineSegment(sketch, "E172", {"start": v(-599.5, 155.18) * mm, "end": v(-599.5, 145.18) * mm, "construction": true});
            skText(sketch, "E173", { "text": "K", "fontName": "AllertaStencil-Regular.ttf"});
            skText(sketch, "E174", { "text": "i", "fontName": "OpenSans-Regular.ttf"});
            skText(sketch, "E175", { "text": "n", "fontName": "AllertaStencil-Regular.ttf"});
            skText(sketch, "E176", { "text": "g", "fontName": "AllertaStencil-Regular.ttf"});
            skText(sketch, "E177", { "text": "R", "fontName": "AllertaStencil-Regular.ttf"});
            skText(sketch, "E178", { "text": "i", "fontName": "AllertaStencil-Regular.ttf"});
            skText(sketch, "E179", { "text": "c", "fontName": "AllertaStencil-Regular.ttf"});
            skText(sketch, "E180", { "text": "h", "fontName": "AllertaStencil-Regular.ttf"});
            skText(sketch, "E181", { "text": "a", "fontName": "AllertaStencil-Regular.ttf"});
            skText(sketch, "E182", { "text": "r", "fontName": "AllertaStencil-Regular.ttf"});
            skText(sketch, "E183", { "text": "d", "fontName": "AllertaStencil-Regular.ttf"});
            skPoint(sketch, "E184.orphan", {"position": v(-699.5, 898.19) * mm});
            skPoint(sketch, "E185.orphan", {"position": v(-499.5, 898.19) * mm});
            skLineSegment(sketch, "E186", {"start": v(-624.5, 873.19) * mm, "end": v(-624.5, 48.19) * mm});
            skLineSegment(sketch, "E187.MirrorCS", {"start": v(-574.5, 898.19) * mm, "end": v(-574.5, 48.19) * mm});
            skPoint(sketch, "E188.orphan", {"position": v(-649.5, 48.19) * mm});
            skPoint(sketch, "E189.MirrorCS.end.orphan", {"position": v(-549.5, 48.19) * mm});
            skPoint(sketch, "E190.trimOffspring.end.orphan", {"position": v(-549.5, 898.19) * mm});
            skLineSegment(sketch, "E191", {"start": v(-624.5, 873.19) * mm, "end": v(-574.5, 873.19) * mm});
            skPoint(sketch, "E191.startSnap0", {"position": v(-599.5, 873.19) * mm});
            skPoint(sketch, "E147.bottom.end.orphan", {"position": v(-624.5, 898.19) * mm});
            skPoint(sketch, "E147.bottom.start.orphan", {"position": v(-649.5, 898.19) * mm});
            const initialGuessF35  = {"E173": [-0.62272, 0.79518, 1, 0, 0.05078], "E174": [-0.609, 0.73518, 1, 0, 0.05], "E175": [-0.62047, 0.67518, 1, 0, 0.05], "E176": [-0.6209, 0.61518, 1, 0, 0.05], "E177": [-0.6217, 0.51518, 1, 0, 0.05], "E178": [-0.60934, 0.45518, 1, 0, 0.05], "E179": [-0.6195, 0.39518, 1, 0, 0.05], "E180": [-0.62082, 0.33518, 1, 0, 0.05], "E181": [-0.62, 0.27518, 1, 0, 0.05], "E182": [-0.61566, 0.21518, 1, 0, 0.05], "E183": [-0.6204, 0.15518, 1, 0, 0.05]};
            skSetInitialGuess(sketch, initialGuessF35);
            skSolve(sketch);
        }
        {
            var Q0;
            Q0 = qSketchRegion(id + "F35", true);
            extrude(context, id + "F36", {"entities" : qUnion([Q0]), "oppositeDirection" : true, "depth" : 50 * mm});
        }
        {
            var Q0;
            Q0=makeQuery(id+"F36.opExtrude","SWEPT_FACE",FACE,{"disambiguationData":[OSD([sQuery(id+"F35.wireOp",EDGE,"E191")])]});
            var sketch = newSketch(context, id + "F37", { "sketchPlane" : qUnion([Q0])});
            skLineSegment(sketch, "E192.0", {"start": v(-50, -622.5) * mm, "end": v(-2, -622.5) * mm});
            skLineSegment(sketch, "E192.1", {"start": v(-2, -622.5) * mm, "end": v(-2, -576.5) * mm});
            skLineSegment(sketch, "E192.2", {"start": v(-50, -576.5) * mm, "end": v(-2, -576.5) * mm});
            skLineSegment(sketch, "E193", {"start": v(-50, -576.5) * mm, "end": v(-50, -622.5) * mm});
            skSolve(sketch);
        }
        {
            var Q0;
            Q0 = qSketchRegion(id + "F37", true);
            extrude(context, id + "F38", {"entities" : qUnion([Q0]), "operationType" : NewBodyOperationType.REMOVE, "endBound" : BoundingType.THROUGH_ALL, "oppositeDirection" : true, "depth" : 25 * mm});
        }
        {
            var Q0;
            Q0=makeQuery(id+"F7.opExtrude","SWEPT_FACE",FACE,{"disambiguationData":[OSD([sQuery(id+"F6.wireOp",EDGE,"E46.bottom")])]});
            var sketch = newSketch(context, id + "F39", { "sketchPlane" : qUnion([Q0])});
            skLineSegment(sketch, "E194.bottom", {"start": v(-1, 0) * mm, "end": v(760, 0) * mm});
            skLineSegment(sketch, "E194.top", {"start": v(-1, 465) * mm, "end": v(800, 465) * mm});
            skLineSegment(sketch, "E194.left", {"start": v(-3, 2) * mm, "end": v(-3, 463) * mm});
            skLineSegment(sketch, "E194.right", {"start": v(802, 75) * mm, "end": v(802, 463) * mm});
            skText(sketch, "E195", { "text": "Fixby Park Works", "fontName": "AllertaStencil-Regular.ttf"});
            skLineSegment(sketch, "E196", {"start": v(402.5, 465) * mm, "end": v(401.32, 0) * mm, "construction": true});
            skText(sketch, "E197", { "text": "Breakdown Gang", "fontName": "AllertaStencil-Regular.ttf"});
            skText(sketch, "E198", { "text": "Crane No1", "fontName": "AllertaStencil-Regular.ttf"});
            skPoint(sketch, "E199.visualSharp", {"position": v(802, 465) * mm});
            skArc(sketch, "E199.filletArc", {"start": v(802, 463) * mm, "mid": v(801.41, 464.41) * mm, "end": v(800, 465) * mm});
            skPoint(sketch, "E200.visualSharp", {"position": v(802, 0) * mm});
            skPoint(sketch, "E201.visualSharp", {"position": v(-3, 465) * mm});
            skArc(sketch, "E201.filletArc", {"start": v(-1, 465) * mm, "mid": v(-2.41, 464.41) * mm, "end": v(-3, 463) * mm});
            skPoint(sketch, "E202.MirrorP", {"position": v(763, 68.17) * mm});
            skPoint(sketch, "E203.MirrorP", {"position": v(806, 67.96) * mm});
            skPoint(sketch, "E204.MirrorP", {"position": v(762.64, -1.83) * mm});
            skPoint(sketch, "E205.orphan", {"position": v(-3, 70) * mm});
            skPoint(sketch, "E206.orphan", {"position": v(40, 0) * mm});
            skPoint(sketch, "E207.visualSharp", {"position": v(-3, 0) * mm});
            skArc(sketch, "E207.filletArc", {"start": v(-3, 2) * mm, "mid": v(-2.41, 0.59) * mm, "end": v(-1, 0) * mm});
            skLineSegment(sketch, "E208", {"start": v(800, 73) * mm, "end": v(767, 73) * mm});
            skLineSegment(sketch, "E209", {"start": v(762, 68) * mm, "end": v(762, 2) * mm});
            skPoint(sketch, "E210.newPointA", {"position": v(762, 3) * mm});
            skArc(sketch, "E210.filletArc", {"start": v(760, 0) * mm, "mid": v(761.41, 0.59) * mm, "end": v(762, 2) * mm});
            skPoint(sketch, "E211.newPointB", {"position": v(802, 73) * mm});
            skArc(sketch, "E211.filletArc", {"start": v(800, 73) * mm, "mid": v(801.41, 73.59) * mm, "end": v(802, 75) * mm});
            skPoint(sketch, "E212.visualSharp", {"position": v(762, 73) * mm});
            skArc(sketch, "E212.filletArc", {"start": v(767, 73) * mm, "mid": v(763.46, 71.54) * mm, "end": v(762, 68) * mm});
            const initialGuessF39  = {"E195": [0.03673, 0.33513, 1, 0, 0.06], "E197": [0.04793, 0.22513, 1, 0, 0.06], "E198": [0.19516, 0.11513, 1, 0, 0.06]};
            skSetInitialGuess(sketch, initialGuessF39);
            skSolve(sketch);
        }
        {
            var Q0;
            Q0 = qSketchRegion(id + "F39", true);
            extrude(context, id + "F40", {"entities" : qUnion([Q0]), "depth" : 2 * mm, "offsetDistance" : 25 * mm});
        }
        {
            var Q0;
            Q0=qCreatedBy(makeId("Front.planeOp"),FACE);
            var sketch = newSketch(context, id + "F41", { "sketchPlane" : qUnion([Q0])});
            skLineSegment(sketch, "E213.bottom", {"start": v(1208.11, 15.86) * mm, "end": v(1794.11, 15.86) * mm});
            skLineSegment(sketch, "E213.top", {"start": v(1208.11, -389.14) * mm, "end": v(1794.11, -389.14) * mm});
            skLineSegment(sketch, "E213.left", {"start": v(1206.11, 13.86) * mm, "end": v(1206.11, -387.14) * mm});
            skLineSegment(sketch, "E213.right", {"start": v(1796.11, 13.86) * mm, "end": v(1796.11, -387.14) * mm});
            skPoint(sketch, "E214.visualSharp", {"position": v(1206.11, 15.86) * mm});
            skArc(sketch, "E214.filletArc", {"start": v(1208.11, 15.86) * mm, "mid": v(1206.7, 15.27) * mm, "end": v(1206.11, 13.86) * mm});
            skPoint(sketch, "E215.visualSharp", {"position": v(1796.11, 15.86) * mm});
            skArc(sketch, "E215.filletArc", {"start": v(1796.11, 13.86) * mm, "mid": v(1795.53, 15.27) * mm, "end": v(1794.11, 15.86) * mm});
            skPoint(sketch, "E216.visualSharp", {"position": v(1796.11, -389.14) * mm});
            skArc(sketch, "E216.filletArc", {"start": v(1794.11, -389.14) * mm, "mid": v(1795.53, -388.56) * mm, "end": v(1796.11, -387.14) * mm});
            skPoint(sketch, "E217.visualSharp", {"position": v(1206.11, -389.14) * mm});
            skArc(sketch, "E217.filletArc", {"start": v(1206.11, -387.14) * mm, "mid": v(1206.7, -388.56) * mm, "end": v(1208.11, -389.14) * mm});
            skLineSegment(sketch, "E218", {"start": v(1206.11, -139.14) * mm, "end": v(1276.11, -139.14) * mm, "construction": true});
            skLineSegment(sketch, "E219", {"start": v(1276.11, -139.14) * mm, "end": v(1276.11, -389.14) * mm, "construction": true});
            skLineSegment(sketch, "E220.bottom", {"start": v(1281.11, -139.14) * mm, "end": v(1301.11, -139.14) * mm});
            skLineSegment(sketch, "E220.top", {"start": v(1281.11, -49.14) * mm, "end": v(1301.11, -49.14) * mm});
            skLineSegment(sketch, "E220.left", {"start": v(1276.11, -134.14) * mm, "end": v(1276.11, -54.14) * mm});
            skLineSegment(sketch, "E220.right", {"start": v(1306.11, -134.14) * mm, "end": v(1306.11, -54.14) * mm});
            skPoint(sketch, "E221.visualSharp", {"position": v(1276.11, -49.14) * mm});
            skArc(sketch, "E221.filletArc", {"start": v(1281.11, -49.14) * mm, "mid": v(1277.58, -50.6) * mm, "end": v(1276.11, -54.14) * mm});
            skPoint(sketch, "E222.visualSharp", {"position": v(1276.11, -139.14) * mm});
            skArc(sketch, "E222.filletArc", {"start": v(1276.11, -134.14) * mm, "mid": v(1277.58, -137.68) * mm, "end": v(1281.11, -139.14) * mm});
            skPoint(sketch, "E223.visualSharp", {"position": v(1306.11, -139.14) * mm});
            skArc(sketch, "E223.filletArc", {"start": v(1301.11, -139.14) * mm, "mid": v(1304.65, -137.68) * mm, "end": v(1306.11, -134.14) * mm});
            skPoint(sketch, "E224.visualSharp", {"position": v(1306.11, -49.14) * mm});
            skArc(sketch, "E224.filletArc", {"start": v(1306.11, -54.14) * mm, "mid": v(1304.65, -50.6) * mm, "end": v(1301.11, -49.14) * mm});
            skSolve(sketch);
        }
        {
            var Q0;
            Q0 = qSketchRegion(id + "F41", true);
            extrude(context, id + "F42", {"entities" : qUnion([Q0]), "depth" : 2 * mm, "offsetDistance" : 25 * mm});
        }
        {
            var Q0;
            Q0=qCreatedBy(makeId("Front.planeOp"),FACE);
            var sketch = newSketch(context, id + "F43", { "sketchPlane" : qUnion([Q0])});
            skLineSegment(sketch, "E225.bottom", {"start": v(250.22, 108.67) * mm, "end": v(788.15, 108.67) * mm});
            skLineSegment(sketch, "E225.top", {"start": v(208.15, -353.33) * mm, "end": v(788.15, -353.33) * mm});
            skLineSegment(sketch, "E225.left", {"start": v(203.15, 61.6) * mm, "end": v(203.15, -348.33) * mm});
            skLineSegment(sketch, "E225.right", {"start": v(793.15, 103.67) * mm, "end": v(793.15, -348.33) * mm});
            skPoint(sketch, "E226.visualSharp", {"position": v(203.15, -353.33) * mm});
            skArc(sketch, "E226.filletArc", {"start": v(203.15, -348.33) * mm, "mid": v(204.61, -351.87) * mm, "end": v(208.15, -353.33) * mm});
            skPoint(sketch, "E227.visualSharp", {"position": v(793.15, -353.33) * mm});
            skArc(sketch, "E227.filletArc", {"start": v(788.15, -353.33) * mm, "mid": v(791.68, -351.87) * mm, "end": v(793.15, -348.33) * mm});
            skPoint(sketch, "E228.visualSharp", {"position": v(793.15, 108.67) * mm});
            skArc(sketch, "E228.filletArc", {"start": v(793.15, 103.67) * mm, "mid": v(791.68, 107.2) * mm, "end": v(788.15, 108.67) * mm});
            skLineSegment(sketch, "E229", {"start": v(204.61, 65.13) * mm, "end": v(246.68, 107.2) * mm});
            skArc(sketch, "E230.filletArc", {"start": v(250.22, 108.67) * mm, "mid": v(248.3, 108.29) * mm, "end": v(246.68, 107.2) * mm});
            skPoint(sketch, "E231.visualSharp", {"position": v(203.15, 63.67) * mm});
            skArc(sketch, "E231.filletArc", {"start": v(204.61, 65.13) * mm, "mid": v(203.53, 63.51) * mm, "end": v(203.15, 61.6) * mm});
            skSolve(sketch);
        }
        {
            var Q0;
            Q0 = qSketchRegion(id + "F43", true);
            extrude(context, id + "F44", {"entities" : qUnion([Q0]), "depth" : 2 * mm, "offsetDistance" : 25 * mm});
        }
        {
            var Q0;
            Q0=qCreatedBy(makeId("Front.planeOp"),FACE);
            var sketch = newSketch(context, id + "F45", { "sketchPlane" : qUnion([Q0])});
            skLineSegment(sketch, "E232.bottom", {"start": v(-1223.5, 239.15) * mm, "end": v(-508.5, 239.15) * mm});
            skLineSegment(sketch, "E232.top", {"start": v(-1223.5, -190.85) * mm, "end": v(-508.5, -190.85) * mm});
            skLineSegment(sketch, "E232.left", {"start": v(-1228.5, 234.15) * mm, "end": v(-1228.5, -185.85) * mm});
            skLineSegment(sketch, "E232.right", {"start": v(-488.5, 219.15) * mm, "end": v(-488.5, -170.85) * mm});
            skPoint(sketch, "E233.visualSharp", {"position": v(-1228.5, 239.15) * mm});
            skArc(sketch, "E233.filletArc", {"start": v(-1223.5, 239.15) * mm, "mid": v(-1227.04, 237.69) * mm, "end": v(-1228.5, 234.15) * mm});
            skPoint(sketch, "E234.visualSharp", {"position": v(-1228.5, -190.85) * mm});
            skArc(sketch, "E234.filletArc", {"start": v(-1228.5, -185.85) * mm, "mid": v(-1227.04, -189.38) * mm, "end": v(-1223.5, -190.85) * mm});
            skPoint(sketch, "E235.visualSharp", {"position": v(-488.5, -190.85) * mm});
            skArc(sketch, "E235.filletArc", {"start": v(-508.5, -190.85) * mm, "mid": v(-494.36, -184.99) * mm, "end": v(-488.5, -170.85) * mm});
            skPoint(sketch, "E236.visualSharp", {"position": v(-488.5, 239.15) * mm});
            skArc(sketch, "E236.filletArc", {"start": v(-488.5, 219.15) * mm, "mid": v(-494.36, 233.3) * mm, "end": v(-508.5, 239.15) * mm});
            skText(sketch, "E237", { "text": "Richard\nOastler", "fontName": "AllertaStencil-Regular.ttf"});
            const initialGuessF45  = {"E237": [-0.85591, 0.1096, 1, 0, 0.05]};
            skSetInitialGuess(sketch, initialGuessF45);
            skSolve(sketch);
        }
        {
            var Q0;
            Q0 = qSketchRegion(id + "F45", true);
            extrude(context, id + "F46", {"entities" : qUnion([Q0]), "depth" : 2 * mm, "offsetDistance" : 25 * mm});
        }
        {
            var Q0;
            Q0=qCreatedBy(makeId("Front.planeOp"),FACE);
            var sketch = newSketch(context, id + "F47", { "sketchPlane" : qUnion([Q0])});
            skLineSegment(sketch, "E238.bottom", {"start": v(-2122.51, 103.14) * mm, "end": v(-1622.51, 103.14) * mm});
            skLineSegment(sketch, "E238.top", {"start": v(-2122.51, -466.86) * mm, "end": v(-1622.51, -466.86) * mm});
            skLineSegment(sketch, "E238.left", {"start": v(-2142.51, 83.14) * mm, "end": v(-2142.51, -446.86) * mm});
            skLineSegment(sketch, "E238.right", {"start": v(-1602.51, 83.14) * mm, "end": v(-1602.51, -446.86) * mm});
            skPoint(sketch, "E239.visualSharp", {"position": v(-2142.51, 103.14) * mm});
            skArc(sketch, "E239.filletArc", {"start": v(-2122.51, 103.14) * mm, "mid": v(-2136.65, 97.28) * mm, "end": v(-2142.51, 83.14) * mm});
            skPoint(sketch, "E240.visualSharp", {"position": v(-2142.51, -466.86) * mm});
            skArc(sketch, "E240.filletArc", {"start": v(-2142.51, -446.86) * mm, "mid": v(-2136.65, -461) * mm, "end": v(-2122.51, -466.86) * mm});
            skPoint(sketch, "E241.visualSharp", {"position": v(-1602.51, -466.86) * mm});
            skArc(sketch, "E241.filletArc", {"start": v(-1622.51, -466.86) * mm, "mid": v(-1608.37, -461) * mm, "end": v(-1602.51, -446.86) * mm});
            skPoint(sketch, "E242.visualSharp", {"position": v(-1602.51, 103.14) * mm});
            skArc(sketch, "E242.filletArc", {"start": v(-1602.51, 83.14) * mm, "mid": v(-1608.37, 97.28) * mm, "end": v(-1622.51, 103.14) * mm});
            skLineSegment(sketch, "E243", {"start": v(-1872.51, 103.14) * mm, "end": v(-1872.51, -466.86) * mm, "construction": true});
            skText(sketch, "E244", { "text": "No1", "fontName": "AllertaStencil-Regular.ttf"});
            const initialGuessF47  = {"E244": [-1.99354, -0.18186, 1, 0, 0.1]};
            skSetInitialGuess(sketch, initialGuessF47);
            skSolve(sketch);
        }
        {
            var Q0;
            Q0 = qSketchRegion(id + "F47", true);
            extrude(context, id + "F48", {"entities" : qUnion([Q0]), "depth" : 2 * mm, "offsetDistance" : 25 * mm});
        }
        {
            var Q0;
            Q0=makeQuery(id+"F48.opExtrude","CAP_FACE",FACE,{"disambiguationData":[OSD([sQuery(id+"F47.wireOp",EDGE,"E238.bottom"),sQuery(id+"F47.wireOp",EDGE,"E238.top"),sQuery(id+"F47.wireOp",EDGE,"E238.left"),sQuery(id+"F47.wireOp",EDGE,"E238.right"),sQuery(id+"F47.wireOp",EDGE,"E239.filletArc"),sQuery(id+"F47.wireOp",EDGE,"E240.filletArc"),sQuery(id+"F47.wireOp",EDGE,"E241.filletArc"),sQuery(id+"F47.wireOp",EDGE,"E242.filletArc"),sQuery(id+"F47.wireOp",EDGE,"E244.sketch_text.stroke-0"),sQuery(id+"F47.wireOp",EDGE,"E244.sketch_text.stroke-1"),sQuery(id+"F47.wireOp",EDGE,"E244.sketch_text.stroke-2"),sQuery(id+"F47.wireOp",EDGE,"E244.sketch_text.stroke-3"),sQuery(id+"F47.wireOp",EDGE,"E244.sketch_text.stroke-4"),sQuery(id+"F47.wireOp",EDGE,"E244.sketch_text.stroke-5"),sQuery(id+"F47.wireOp",EDGE,"E244.sketch_text.stroke-6"),sQuery(id+"F47.wireOp",EDGE,"E244.sketch_text.stroke-7"),sQuery(id+"F47.wireOp",EDGE,"E244.sketch_text.stroke-8"),sQuery(id+"F47.wireOp",EDGE,"E244.sketch_text.stroke-9"),sQuery(id+"F47.wireOp",EDGE,"E244.sketch_text.stroke-10"),sQuery(id+"F47.wireOp",EDGE,"E244.sketch_text.stroke-11"),sQuery(id+"F47.wireOp",EDGE,"E244.sketch_text.stroke-12"),sQuery(id+"F47.wireOp",EDGE,"E244.sketch_text.stroke-13"),sQuery(id+"F47.wireOp",EDGE,"E244.sketch_text.stroke-14"),sQuery(id+"F47.wireOp",EDGE,"E244.sketch_text.stroke-15"),sQuery(id+"F47.wireOp",EDGE,"E244.sketch_text.stroke-16"),sQuery(id+"F47.wireOp",EDGE,"E244.sketch_text.stroke-17"),sQuery(id+"F47.wireOp",EDGE,"E244.sketch_text.stroke-18"),sQuery(id+"F47.wireOp",EDGE,"E244.sketch_text.stroke-19"),sQuery(id+"F47.wireOp",EDGE,"E244.sketch_text.stroke-20"),sQuery(id+"F47.wireOp",EDGE,"E244.sketch_text.stroke-21"),sQuery(id+"F47.wireOp",EDGE,"E244.sketch_text.stroke-22"),sQuery(id+"F47.wireOp",EDGE,"E244.sketch_text.stroke-23"),sQuery(id+"F47.wireOp",EDGE,"E244.sketch_text.stroke-24"),sQuery(id+"F47.wireOp",EDGE,"E244.sketch_text.stroke-25"),sQuery(id+"F47.wireOp",EDGE,"E244.sketch_text.stroke-26"),sQuery(id+"F47.wireOp",EDGE,"E244.sketch_text.stroke-27"),sQuery(id+"F47.wireOp",EDGE,"E244.sketch_text.stroke-28"),sQuery(id+"F47.wireOp",EDGE,"E244.sketch_text.stroke-29"),sQuery(id+"F47.wireOp",EDGE,"E244.sketch_text.stroke-30"),sQuery(id+"F47.wireOp",EDGE,"E244.sketch_text.stroke-31"),sQuery(id+"F47.wireOp",EDGE,"E244.sketch_text.stroke-32"),sQuery(id+"F47.wireOp",EDGE,"E244.sketch_text.stroke-33"),sQuery(id+"F47.wireOp",EDGE,"E244.sketch_text.stroke-34"),sQuery(id+"F47.wireOp",EDGE,"E244.sketch_text.stroke-35"),sQuery(id+"F47.wireOp",EDGE,"E244.sketch_text.stroke-36"),sQuery(id+"F47.wireOp",EDGE,"E244.sketch_text.stroke-37"),sQuery(id+"F47.wireOp",EDGE,"E244.sketch_text.stroke-38"),sQuery(id+"F47.wireOp",EDGE,"E244.sketch_text.stroke-39"),sQuery(id+"F47.wireOp",EDGE,"E244.sketch_text.stroke-40"),sQuery(id+"F47.wireOp",EDGE,"E244.sketch_text.stroke-41"),sQuery(id+"F47.wireOp",EDGE,"E244.sketch_text.stroke-42"),sQuery(id+"F47.wireOp",EDGE,"E244.sketch_text.stroke-43"),sQuery(id+"F47.wireOp",EDGE,"E244.sketch_text.stroke-44"),sQuery(id+"F47.wireOp",EDGE,"E244.sketch_text.stroke-45"),sQuery(id+"F47.wireOp",EDGE,"E244.sketch_text.stroke-46"),sQuery(id+"F47.wireOp",EDGE,"E244.sketch_text.stroke-47"),sQuery(id+"F47.wireOp",EDGE,"E244.sketch_text.stroke-48"),sQuery(id+"F47.wireOp",EDGE,"E244.sketch_text.stroke-49")])],"isStart":false});
            var sketch = newSketch(context, id + "F49", { "sketchPlane" : qUnion([Q0])});
            skLineSegment(sketch, "E245.bottom", {"start": v(-1667.88, 376.45) * mm, "end": v(-1655.18, 376.45) * mm});
            skLineSegment(sketch, "E245.top", {"start": v(-1662.88, 351.45) * mm, "end": v(-1660.18, 351.45) * mm});
            skLineSegment(sketch, "E245.left", {"start": v(-1667.88, 376.45) * mm, "end": v(-1667.88, 356.45) * mm});
            skLineSegment(sketch, "E245.right", {"start": v(-1655.18, 376.45) * mm, "end": v(-1655.18, 356.45) * mm});
            skLineSegment(sketch, "E246", {"start": v(-1661.53, 376.45) * mm, "end": v(-1661.53, 351.45) * mm, "construction": true});
            skLineSegment(sketch, "E247", {"start": v(-1661.53, 351.45) * mm, "end": v(-1661.53, 357.45) * mm, "construction": true});
            skCircle(sketch, "E248", {"center": v(-1661.53, 357.45) * mm, "radius": 2.5 * mm});
            skPoint(sketch, "E249.visualSharp", {"position": v(-1655.18, 351.45) * mm});
            skArc(sketch, "E249.filletArc", {"start": v(-1660.18, 351.45) * mm, "mid": v(-1656.65, 352.92) * mm, "end": v(-1655.18, 356.45) * mm});
            skPoint(sketch, "E250.visualSharp", {"position": v(-1667.88, 351.45) * mm});
            skArc(sketch, "E250.filletArc", {"start": v(-1667.88, 356.45) * mm, "mid": v(-1666.42, 352.92) * mm, "end": v(-1662.88, 351.45) * mm});
            skSolve(sketch);
        }
        {
            var Q0;
            Q0 = qSketchRegion(id + "F49", true);
            extrude(context, id + "F50", {"entities" : qUnion([Q0]), "depth" : 3 * mm, "offsetDistance" : 25 * mm});
        }
    });